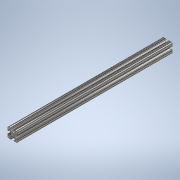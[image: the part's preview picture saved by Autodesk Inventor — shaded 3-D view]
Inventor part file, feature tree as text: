
AUTODESK INVENTOR PART (.ipt)
format: ipt  version: 2020 (Build 240168000, 168)  size: 240,128 bytes
history: native  units: in
note: dims shown in document units (in); Inventor stores cm internally (conversion verified against a paired STEP export)
features: extrude x1, sketch x1
ambient origin geometry x8: Origin, YZ Plane, XZ Plane, XY Plane, X Axis, Y Axis, Z Axis, Center Point
bodies: Solid1 (feature_tree)
feature tree (2):
  extrude  "Extrusion1"  [1 undecoded]
  sketch  "Sketch1"  dims[d0=16.0in d1=0.0in]
note: 1 required parameter value undecoded (feature->parameter linkage not recoverable at this tier; creation-order binding heuristic only, values carry confidence <= 0.55)
